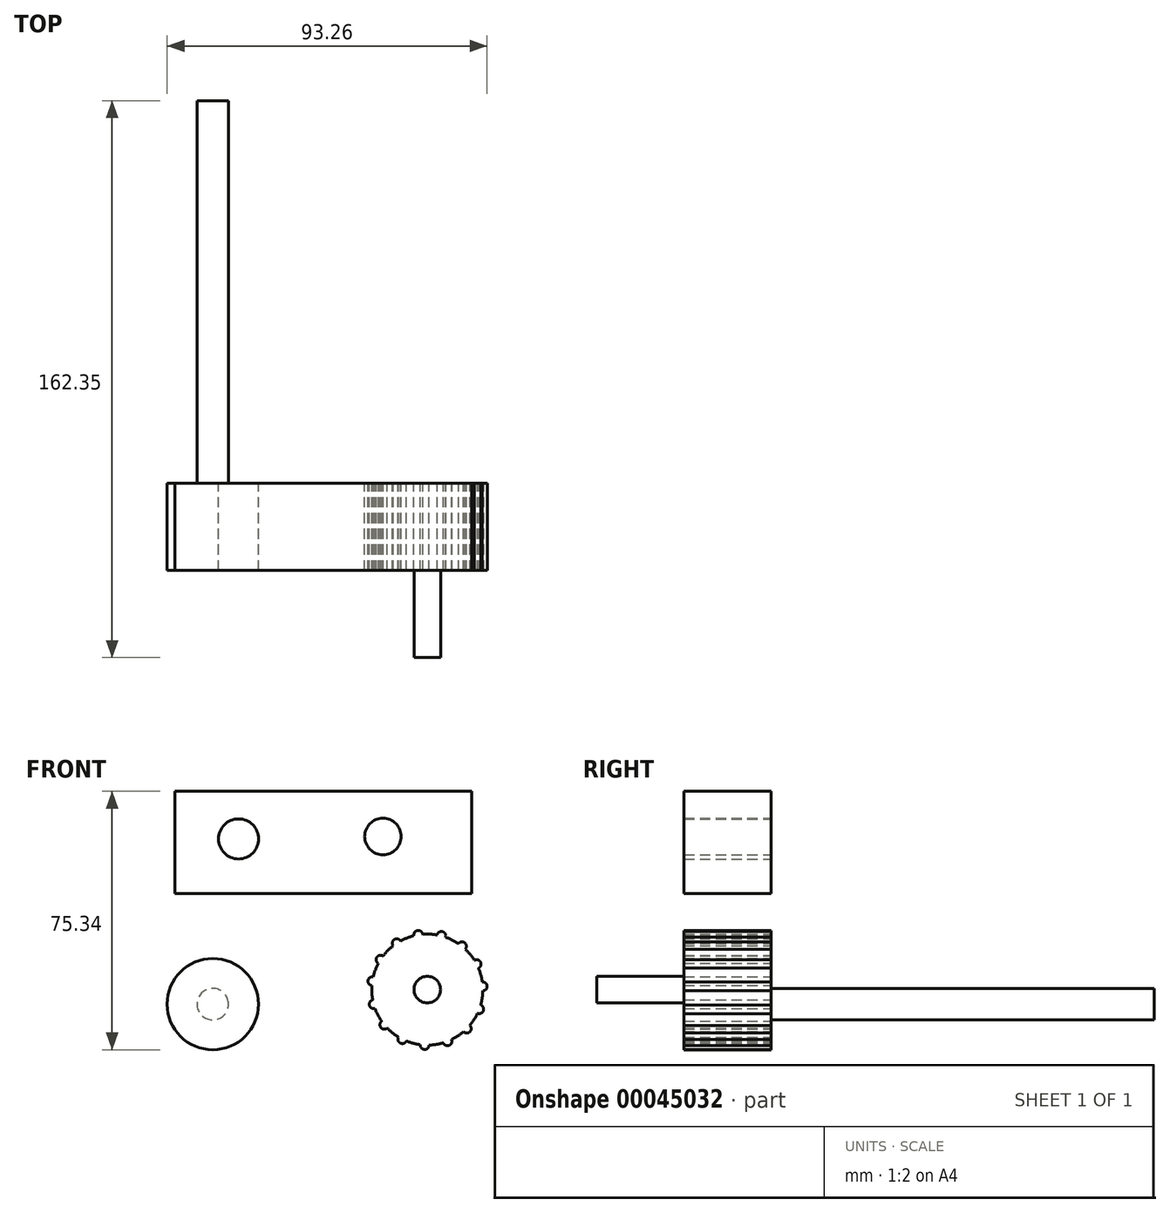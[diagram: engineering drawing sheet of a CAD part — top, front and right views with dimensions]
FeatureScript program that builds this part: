
annotation { "Feature Type Name" : "Feature", "Feature Type Description" : "" }
export const myFeature = defineFeature(function(context is Context, id is Id, definition is map)
    precondition{}
    {
        {
            var Q0;
            Q0=qCreatedBy(makeId("Front.planeOp"),FACE);
            var sketch = newSketch(context, id + "F0", { "sketchPlane" : qUnion([Q0])});
            skLineSegment(sketch, "E0.bottom", {"start": v(-51.23, 43.59) * mm, "end": v(35.25, 43.59) * mm});
            skLineSegment(sketch, "E0.top", {"start": v(-51.23, 13.75) * mm, "end": v(35.25, 13.75) * mm});
            skLineSegment(sketch, "E0.left", {"start": v(-51.23, 43.59) * mm, "end": v(-51.23, 13.75) * mm});
            skLineSegment(sketch, "E0.right", {"start": v(35.25, 43.59) * mm, "end": v(35.25, 13.75) * mm});
            skCircle(sketch, "E1", {"center": v(-40.18, -18.45) * mm, "radius": 13.3 * mm});
            skCircle(sketch, "E2", {"center": v(-32.66, 29.72) * mm, "radius": 5.84 * mm});
            skCircle(sketch, "E3", {"center": v(9.4, 30.43) * mm, "radius": 5.32 * mm});
            skCircle(sketch, "E4", {"center": v(22.32, -14.22) * mm, "radius": 16.19 * mm});
            skCircle(sketch, "E5", {"center": v(19.7, 1.76) * mm, "radius": 1.29 * mm});
            skCircle(sketch, "E6.1.0", {"center": v(13.43, -0.7) * mm, "radius": 1.29 * mm});
            skCircle(sketch, "E6.2.0", {"center": v(8.7, -5.48) * mm, "radius": 1.29 * mm});
            skCircle(sketch, "E6.3.0", {"center": v(6.32, -11.77) * mm, "radius": 1.29 * mm});
            skCircle(sketch, "E6.4.0", {"center": v(6.71, -18.5) * mm, "radius": 1.29 * mm});
            skCircle(sketch, "E6.5.0", {"center": v(9.8, -24.47) * mm, "radius": 1.29 * mm});
            skCircle(sketch, "E6.6.0", {"center": v(15.06, -28.68) * mm, "radius": 1.29 * mm});
            skCircle(sketch, "E6.7.0", {"center": v(21.57, -30.38) * mm, "radius": 1.29 * mm});
            skCircle(sketch, "E6.8.0", {"center": v(28.2, -29.3) * mm, "radius": 1.29 * mm});
            skCircle(sketch, "E6.9.0", {"center": v(33.83, -25.6) * mm, "radius": 1.29 * mm});
            skCircle(sketch, "E6.10.0", {"center": v(37.47, -19.93) * mm, "radius": 1.29 * mm});
            skCircle(sketch, "E6.11.0", {"center": v(38.48, -13.28) * mm, "radius": 1.29 * mm});
            skCircle(sketch, "E6.12.0", {"center": v(36.7, -6.79) * mm, "radius": 1.29 * mm});
            skCircle(sketch, "E6.13.0", {"center": v(32.44, -1.58) * mm, "radius": 1.29 * mm});
            skCircle(sketch, "E6.14.0", {"center": v(26.42, 1.44) * mm, "radius": 1.29 * mm});
            skSolve(sketch);
        }
        {
            var Q0;
            Q0=makeQuery(id+"F0.imprint","IMPRINT",FACE,{"disambiguationData":[TD([[makeQuery(id+"F0.imprint","IMPRINT",EDGE,{"derivedFrom":sQuery(id+"F0.wireOp",EDGE,"E0.bottom")}),-1.0]])]});
            extrude(context, id + "F1", {"entities" : qUnion([Q0]), "depth" : 25.4 * mm});
        }
        {
            var Q0;
            Q0 = qSketchRegion(id + "F0", true);
            extrude(context, id + "F2", {"entities" : qUnion([Q0]), "operationType" : NewBodyOperationType.ADD, "depth" : 25.4 * mm});
        }
        {
            var Q0;
            Q0=makeQuery(id+"F2.opExtrude","CAP_FACE",FACE,{"disambiguationData":[OSD([sQuery(id+"F0.wireOp",EDGE,"E1")])],"isStart":true});
            var sketch = newSketch(context, id + "F3", { "sketchPlane" : qUnion([Q0])});
            skCircle(sketch, "E7", {"center": v(40.18, -18.45) * mm, "radius": 4.6 * mm});
            skSolve(sketch);
        }
        {
            var Q0;
            Q0=makeQuery(id+"F3.imprint","IMPRINT",FACE,{"disambiguationData":[TD([[makeQuery(id+"F3.imprint","IMPRINT",EDGE,{"derivedFrom":sQuery(id+"F3.wireOp",EDGE,"E7")}),1.0]])]});
            extrude(context, id + "F4", {"entities" : qUnion([Q0]), "operationType" : NewBodyOperationType.ADD, "depth" : 111.55 * mm});
        }
        {
            var Q0;
            Q0=makeQuery(id+"F2.opExtrude","CAP_FACE",FACE,{"disambiguationData":[OSD([sQuery(id+"F0.wireOp",EDGE,"E4")])],"isStart":false});
            var sketch = newSketch(context, id + "F5", { "sketchPlane" : qUnion([Q0])});
            skCircle(sketch, "E8", {"center": v(22.32, -14.22) * mm, "radius": 3.88 * mm});
            skSolve(sketch);
        }
        {
            var Q0;
            Q0 = qSketchRegion(id + "F5", true);
            extrude(context, id + "F6", {"entities" : qUnion([Q0]), "operationType" : NewBodyOperationType.ADD, "depth" : 25.4 * mm});
        }
    });
